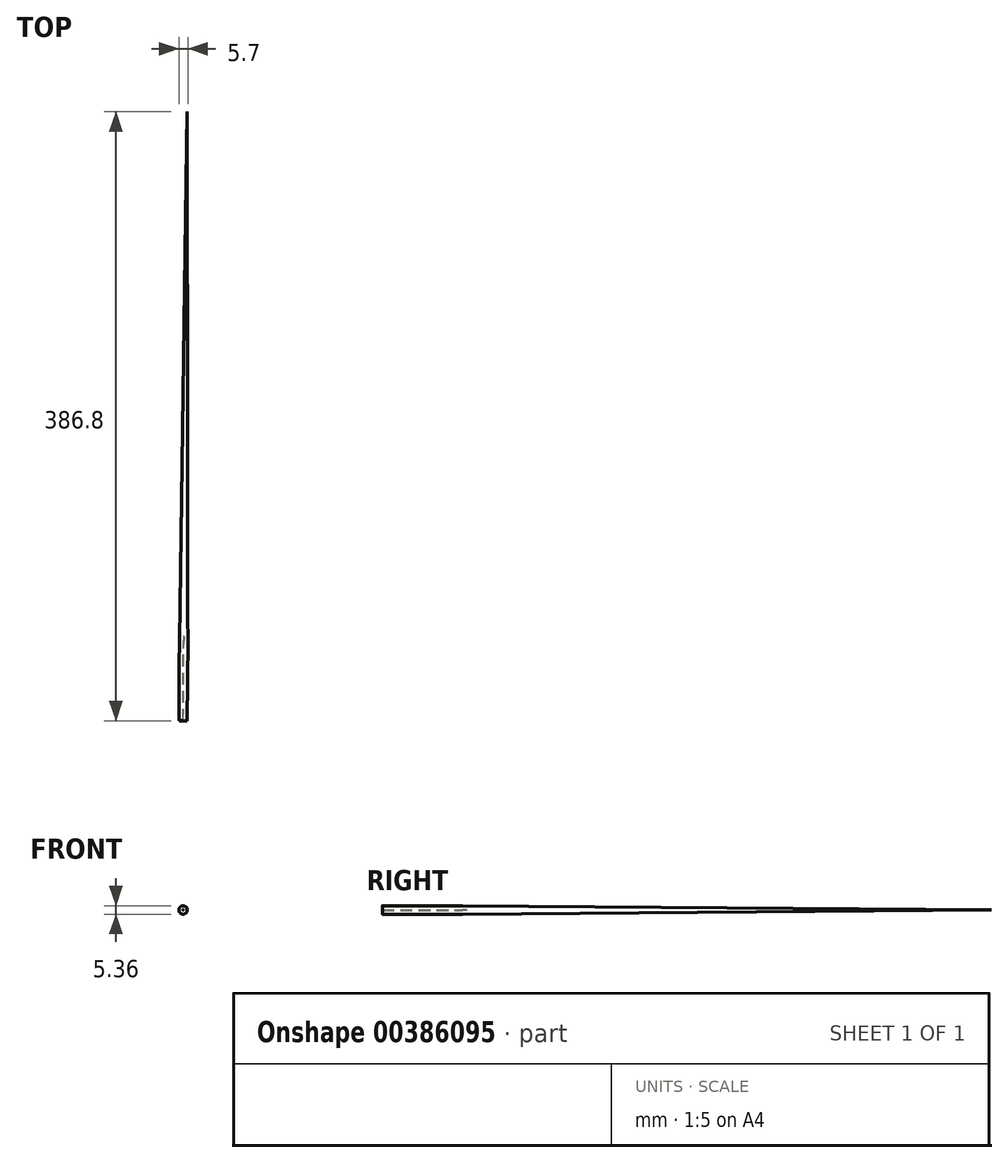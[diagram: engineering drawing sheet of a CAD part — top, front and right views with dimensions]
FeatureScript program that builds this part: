
annotation { "Feature Type Name" : "Feature", "Feature Type Description" : "" }
export const myFeature = defineFeature(function(context is Context, id is Id, definition is map)
    precondition{}
    {
        {
            var Q0;
            Q0=qCreatedBy(makeId("Top.planeOp"),FACE);
            var sketch = newSketch(context, id + "F0", { "sketchPlane" : qUnion([Q0])});
            skArc(sketch, "E0", {"start": v(-6.46, 61.86) * mm, "mid": v(-69.18, 0.4) * mm, "end": v(-7.26, -61.87) * mm});
            skLineSegment(sketch, "E1", {"start": v(-6.4, 71.17) * mm, "end": v(-7.32, -69.65) * mm});
            skArc(sketch, "E2", {"start": v(-6.75, 39.38) * mm, "mid": v(-6.68, 39.38) * mm, "end": v(-6.6, 39.38) * mm});
            skArc(sketch, "E3", {"start": v(-7.11, -38.6) * mm, "mid": v(-7.19, -38.6) * mm, "end": v(-7.26, -38.6) * mm});
            skLineSegment(sketch, "E4", {"start": v(-6.44, 87.56) * mm, "end": v(-7.58, -88.01) * mm});
            skLineSegment(sketch, "E5", {"start": v(-68.65, 8.05) * mm, "end": v(-6.81, 7.65) * mm});
            skLineSegment(sketch, "E6", {"start": v(-6.81, 7.65) * mm, "end": v(-7.08, -10.94) * mm});
            skLineSegment(sketch, "E7", {"start": v(-7.08, -10.94) * mm, "end": v(-68.36, -10.07) * mm});
            skArc(sketch, "E8", {"start": v(-6.8, 8.34) * mm, "mid": v(-8.75, 8.23) * mm, "end": v(-10.62, 7.67) * mm});
            skArc(sketch, "E9.trimOffspring", {"start": v(-7.06, -8.35) * mm, "mid": v(-6.99, -8.35) * mm, "end": v(-6.92, -8.35) * mm});
            skEllipticalArc(sketch, "E10", {});
            const initialGuessF0  = {"E10": [-0.007315199356526136, 0, 0.06061020895686228, 0.9981615112646879, 0.008355127127603827, 0.00813446880104325, 0, 3.252832611415289]};
            skSetInitialGuess(sketch, initialGuessF0);
            skSolve(sketch);
        }
        {
            var Q0;
            {var subQ4=sQuery(id+"F0.wireOp",EDGE,"E7");Q0=makeQuery(id+"F0.imprint","IMPRINT",FACE,{"disambiguationData":[TD([[makeQuery(id+"F0.imprint","IMPRINT",EDGE,{"derivedFrom":subQ4}),-1.0]])]});}
            var Q1;
            {var subQ5=sQuery(id+"F0.wireOp",EDGE,"E2");Q1=makeQuery(id+"F0.imprint","IMPRINT",FACE,{"disambiguationData":[TD([[makeQuery(id+"F0.imprint","IMPRINT",EDGE,{"derivedFrom":subQ5}),1.0]])]});}
            var Q2;
            {var subQ0=sQuery(id+"F0.wireOp",EDGE,"E7");Q2=makeQuery(id+"F0.imprint","IMPRINT",FACE,{"disambiguationData":[TD([[makeQuery(id+"F0.imprint","IMPRINT",EDGE,{"derivedFrom":subQ0}),1.0]])]});}
            var Q3;
            {var subQ0=sQuery(id+"F0.wireOp",EDGE,"E5");var subQ1=sQuery(id+"F0.wireOp",EDGE,"E4");var subQ2=makeQuery(id+"F0.imprint","INTERSECT",VERTEX,{"derivedFrom":[subQ1,subQ0]});Q3=makeQuery(id+"F0.imprint","IMPRINT",FACE,{"disambiguationData":[TD([[makeQuery(id+"F0.imprint","IMPRINT",EDGE,{"disambiguationData":[TD([[subQ2,-1.0]])],"derivedFrom":subQ1}),-1.0]])]});}
            var Q4;
            {var subQ0=sQuery(id+"F0.wireOp",EDGE,"E5");var subQ1=sQuery(id+"F0.wireOp",EDGE,"E0");var subQ2=makeQuery(id+"F0.imprint","INTERSECT",VERTEX,{"derivedFrom":[subQ1,subQ0]});Q4=makeQuery(id+"F0.imprint","IMPRINT",FACE,{"disambiguationData":[TD([[makeQuery(id+"F0.imprint","IMPRINT",EDGE,{"disambiguationData":[TD([[subQ2,1.0]])],"derivedFrom":subQ1}),1.0]])]});}
            var Q5;
            {var subQ0=sQuery(id+"F0.wireOp",EDGE,"E5");var subQ1=sQuery(id+"F0.wireOp",EDGE,"E4");var subQ2=makeQuery(id+"F0.imprint","INTERSECT",VERTEX,{"derivedFrom":[subQ1,subQ0]});Q5=makeQuery(id+"F0.imprint","IMPRINT",FACE,{"disambiguationData":[TD([[makeQuery(id+"F0.imprint","IMPRINT",EDGE,{"disambiguationData":[TD([[subQ2,-1.0]])],"derivedFrom":subQ1}),1.0]])]});}
            var Q6;
            {var subQ5=sQuery(id+"F0.wireOp",EDGE,"E3");Q6=makeQuery(id+"F0.imprint","IMPRINT",FACE,{"disambiguationData":[TD([[makeQuery(id+"F0.imprint","IMPRINT",EDGE,{"derivedFrom":subQ5}),1.0]])]});}
            var Q7;
            {var subQ0=sQuery(id+"F0.wireOp",EDGE,"E2");Q7=makeQuery(id+"F0.imprint","IMPRINT",FACE,{"disambiguationData":[TD([[makeQuery(id+"F0.imprint","IMPRINT",EDGE,{"derivedFrom":subQ0}),-1.0]])]});}
            var Q8;
            {var subQ5=sQuery(id+"F0.wireOp",EDGE,"E3");Q8=makeQuery(id+"F0.imprint","IMPRINT",FACE,{"disambiguationData":[TD([[makeQuery(id+"F0.imprint","IMPRINT",EDGE,{"derivedFrom":subQ5}),-1.0]])]});}
            var Q9;
            {var subQ0=sQuery(id+"F0.wireOp",EDGE,"E8");var subQ1=sQuery(id+"F0.wireOp",EDGE,"E4");var subQ2=makeQuery(id+"F0.imprint","INTERSECT",VERTEX,{"derivedFrom":[subQ1,subQ0]});Q9=makeQuery(id+"F0.imprint","IMPRINT",FACE,{"disambiguationData":[TD([[makeQuery(id+"F0.imprint","IMPRINT",EDGE,{"disambiguationData":[TD([[subQ2,-1.0]])],"derivedFrom":subQ1}),-1.0]])]});}
            var Q10;
            {var subQ1=sQuery(id+"F0.wireOp",EDGE,"E1");var subQ3=sQuery(id+"F0.wireOp",EDGE,"E10");var subQ4=makeQuery(id+"F0.imprint","INTERSECT",VERTEX,{"derivedFrom":[subQ1,subQ3]});Q10=makeQuery(id+"F0.imprint","IMPRINT",FACE,{"disambiguationData":[TD([[makeQuery(id+"F0.imprint","IMPRINT",EDGE,{"disambiguationData":[TD([[subQ4,1.0]])],"derivedFrom":subQ3}),1.0]])]});}
            var Q11;
            {var subQ0=sQuery(id+"F0.wireOp",EDGE,"E10");var subQ1=sQuery(id+"F0.wireOp",EDGE,"E4");var subQ2=makeQuery(id+"F0.imprint","INTERSECT",VERTEX,{"disambiguationData":[OD(0.0)],"derivedFrom":[subQ1,subQ0]});Q11=makeQuery(id+"F0.imprint","IMPRINT",FACE,{"disambiguationData":[TD([[makeQuery(id+"F0.imprint","IMPRINT",EDGE,{"disambiguationData":[TD([[subQ2,-1.0]])],"derivedFrom":subQ1}),-1.0]])]});}
            var Q12;
            {var subQ1=sQuery(id+"F0.wireOp",EDGE,"E4");var subQ3=sQuery(id+"F0.wireOp",EDGE,"E9.trimOffspring");var subQ4=makeQuery(id+"F0.imprint","INTERSECT",VERTEX,{"derivedFrom":[subQ1,subQ3]});Q12=makeQuery(id+"F0.imprint","IMPRINT",FACE,{"disambiguationData":[TD([[makeQuery(id+"F0.imprint","IMPRINT",EDGE,{"disambiguationData":[TD([[subQ4,-1.0]])],"derivedFrom":subQ3}),-1.0]])]});}
            var Q13;
            {var subQ0=sQuery(id+"F0.wireOp",EDGE,"E9.trimOffspring");var subQ1=sQuery(id+"F0.wireOp",EDGE,"E4");var subQ2=makeQuery(id+"F0.imprint","INTERSECT",VERTEX,{"derivedFrom":[subQ1,subQ0]});Q13=makeQuery(id+"F0.imprint","IMPRINT",FACE,{"disambiguationData":[TD([[makeQuery(id+"F0.imprint","IMPRINT",EDGE,{"disambiguationData":[TD([[subQ2,1.0]])],"derivedFrom":subQ1}),1.0]])]});}
            var Q14;
            {var subQ3=sQuery(id+"F0.wireOp",EDGE,"E10");var subQ5=sQuery(id+"F0.wireOp",EDGE,"E4");var subQ6=makeQuery(id+"F0.imprint","INTERSECT",VERTEX,{"disambiguationData":[OD(0.0)],"derivedFrom":[subQ5,subQ3]});Q14=makeQuery(id+"F0.imprint","IMPRINT",FACE,{"disambiguationData":[TD([[makeQuery(id+"F0.imprint","IMPRINT",EDGE,{"disambiguationData":[TD([[subQ6,-1.0]])],"derivedFrom":subQ5}),1.0]])]});}
            var Q15;
            {var subQ0=sQuery(id+"F0.wireOp",EDGE,"E9.trimOffspring");var subQ1=sQuery(id+"F0.wireOp",EDGE,"E1");var subQ2=makeQuery(id+"F0.imprint","INTERSECT",VERTEX,{"derivedFrom":[subQ1,subQ0]});Q15=makeQuery(id+"F0.imprint","IMPRINT",FACE,{"disambiguationData":[TD([[makeQuery(id+"F0.imprint","IMPRINT",EDGE,{"disambiguationData":[TD([[subQ2,1.0]])],"derivedFrom":subQ1}),-1.0]])]});}
            var Q16;
            {var subQ0=sQuery(id+"F0.wireOp",EDGE,"E8");var subQ1=sQuery(id+"F0.wireOp",EDGE,"E4");var subQ2=makeQuery(id+"F0.imprint","INTERSECT",VERTEX,{"derivedFrom":[subQ1,subQ0]});Q16=makeQuery(id+"F0.imprint","IMPRINT",FACE,{"disambiguationData":[TD([[makeQuery(id+"F0.imprint","IMPRINT",EDGE,{"disambiguationData":[TD([[subQ2,-1.0]])],"derivedFrom":subQ1}),1.0]])]});}
            var Q17;
            Q17=sQuery(id+"F0.wireOp",EDGE,"E1");
            revolve(context, id + "F1", {"entities" : qUnion([Q0, Q1, Q2, Q3, Q4, Q5, Q6, Q7, Q8, Q9, Q10, Q11, Q12, Q13, Q14, Q15, Q16]), "axis" : qUnion([Q17]), "revolveType" : RevolveType.FULL});
        }
        {
            var Q0;
            Q0=makeQuery(id+"F1.opRevolve","SWEPT_FACE",FACE,{"disambiguationData":[OSD([sQuery(id+"F0.wireOp",EDGE,"E0")])]});
            shell(context, id + "F2", {"entities" : qUnion([Q0]), "thickness" : 2.54 * mm});
        }
    });
